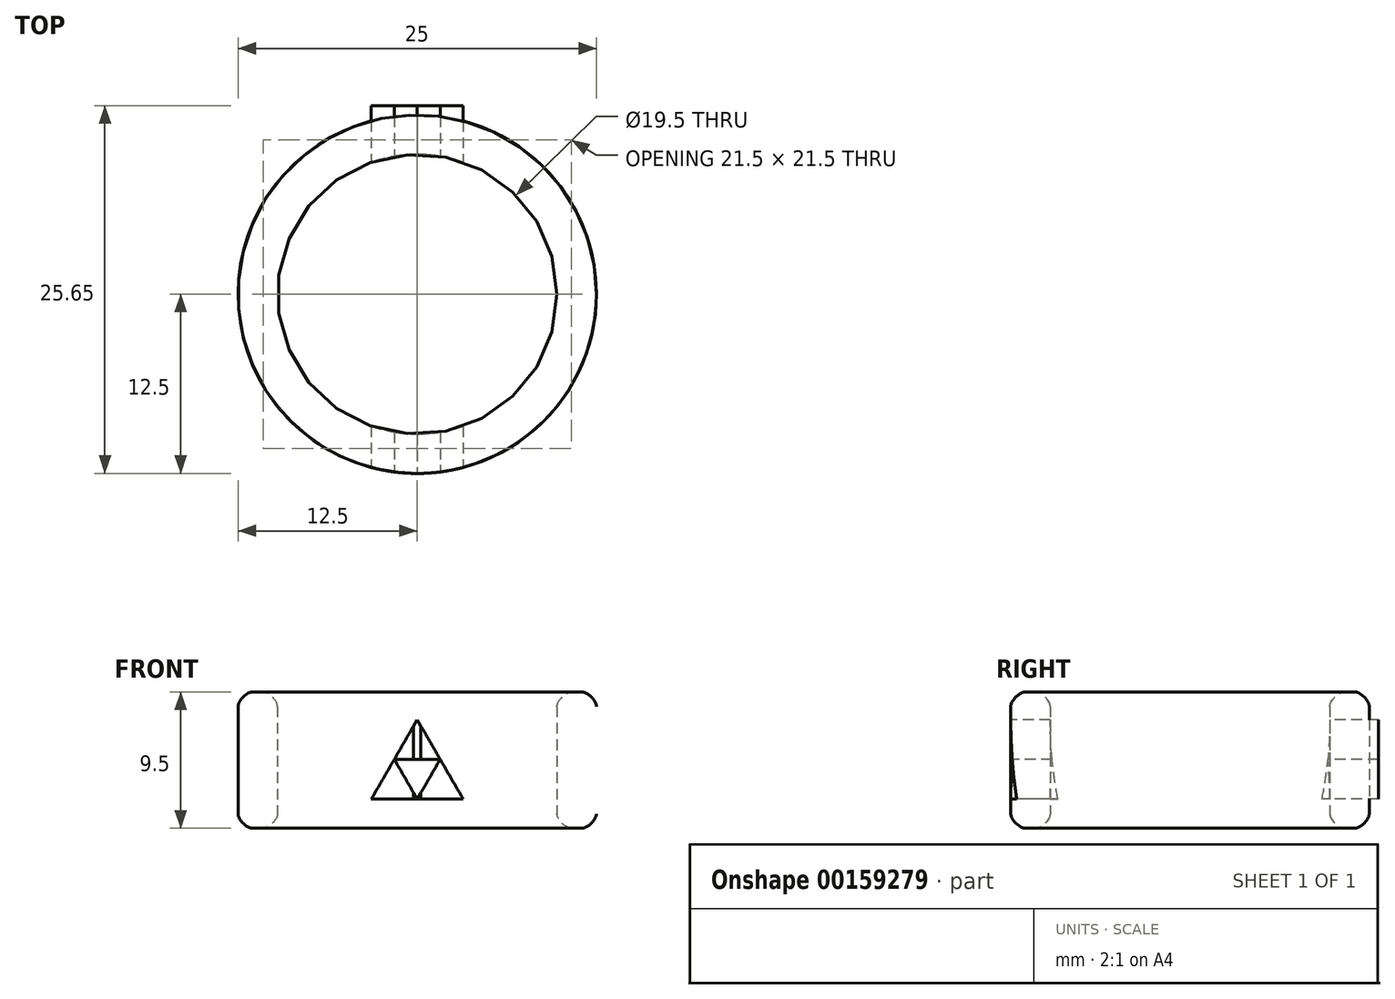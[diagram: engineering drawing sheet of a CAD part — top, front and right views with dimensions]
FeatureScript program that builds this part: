
annotation { "Feature Type Name" : "Feature", "Feature Type Description" : "" }
export const myFeature = defineFeature(function(context is Context, id is Id, definition is map)
    precondition{}
    {
        {
            var Q0;
            Q0=qCreatedBy(makeId("Top.planeOp"),FACE);
            var sketch = newSketch(context, id + "F0", { "sketchPlane" : qUnion([Q0])});
            skPoint(sketch, "E0", {"position": v(0, 12.5) * mm});
            skCircle(sketch, "E1", {"center": v(0, 12.5) * mm, "radius": 9.75 * mm});
            skCircle(sketch, "E2", {"center": v(0, 12.5) * mm, "radius": 12.5 * mm});
            skSolve(sketch);
        }
        {
            var Q0;
            Q0=makeQuery(id+"F0.imprint","IMPRINT",FACE,{"disambiguationData":[TD([[makeQuery(id+"F0.imprint","IMPRINT",EDGE,{"derivedFrom":sQuery(id+"F0.wireOp",EDGE,"E1")}),-1.0]])]});
            extrude(context, id + "F1", {"entities" : qUnion([Q0]), "depth" : 9.5 * mm});
        }
        {
            var Q0;
            Q0=makeQuery(id+"F1.opExtrude","CAP_EDGE",EDGE,{"disambiguationData":[OSD([sQuery(id+"F0.wireOp",EDGE,"E2")])],"isStart":false});
            var Q1;
            Q1=makeQuery(id+"F1.opExtrude","CAP_EDGE",EDGE,{"disambiguationData":[OSD([sQuery(id+"F0.wireOp",EDGE,"E1")])],"isStart":false});
            var Q2;
            Q2=makeQuery(id+"F1.opExtrude","CAP_EDGE",EDGE,{"disambiguationData":[OSD([sQuery(id+"F0.wireOp",EDGE,"E1")])],"isStart":true});
            var Q3;
            Q3=makeQuery(id+"F1.opExtrude","CAP_EDGE",EDGE,{"disambiguationData":[OSD([sQuery(id+"F0.wireOp",EDGE,"E2")])],"isStart":true});
            fillet(context, id + "F2", {"entities" : qUnion([Q0, Q1, Q2, Q3]), "radius" : 1 * mm, "rho" : 0.3, "crossSection" : FilletCrossSection.CONIC, "allowEdgeOverflow" : false});
        }
        {
            var Q0;
            Q0=qCreatedBy(makeId("Front.planeOp"),FACE);
            var sketch = newSketch(context, id + "F3", { "sketchPlane" : qUnion([Q0])});
            skPoint(sketch, "E3", {"position": v(0, 3.88) * mm});
            skCircle(sketch, "E4.cCircle", {"center": v(0, 3.88) * mm, "radius": 1.85 * mm, "construction": true});
            skLineSegment(sketch, "E4.0", {"start": v(3.2, 2.03) * mm, "end": v(-3.2, 2.03) * mm});
            skLineSegment(sketch, "E4.1", {"start": v(-3.2, 2.03) * mm, "end": v(0, 7.58) * mm});
            skLineSegment(sketch, "E4.2", {"start": v(0, 7.58) * mm, "end": v(3.2, 2.03) * mm});
            skPoint(sketch, "E4.0.midPoint", {"position": v(0, 2.03) * mm});
            skCircle(sketch, "E5.cCircle", {"center": v(0, 3.88) * mm, "radius": 0.92 * mm, "construction": true});
            skPoint(sketch, "E5.cCircle.perimeterSnap0", {"position": v(-1.6, 4.8) * mm});
            skLineSegment(sketch, "E5.0", {"start": v(-1.6, 4.8) * mm, "end": v(1.6, 4.8) * mm});
            skLineSegment(sketch, "E5.1", {"start": v(1.6, 4.8) * mm, "end": v(0, 2.03) * mm});
            skLineSegment(sketch, "E5.2", {"start": v(0, 2.03) * mm, "end": v(-1.6, 4.8) * mm});
            skPoint(sketch, "E5.0.midPoint", {"position": v(0, 4.8) * mm});
            skPoint(sketch, "E5.0.midPoint.positionSnap0", {"position": v(-1.6, 4.8) * mm});
            skSolve(sketch);
        }
        {
            var Q0;
            {var subQ3=sQuery(id+"F3.wireOp",EDGE,"E5.1");Q0=makeQuery(id+"F3.imprint","IMPRINT",FACE,{"disambiguationData":[TD([[makeQuery(id+"F3.imprint","IMPRINT",EDGE,{"derivedFrom":subQ3}),1.0]])]});}
            var Q1;
            {var subQ3=sQuery(id+"F3.wireOp",EDGE,"E5.0");Q1=makeQuery(id+"F3.imprint","IMPRINT",FACE,{"disambiguationData":[TD([[makeQuery(id+"F3.imprint","IMPRINT",EDGE,{"derivedFrom":subQ3}),1.0]])]});}
            var Q2;
            {var subQ3=sQuery(id+"F3.wireOp",EDGE,"E5.2");Q2=makeQuery(id+"F3.imprint","IMPRINT",FACE,{"disambiguationData":[TD([[makeQuery(id+"F3.imprint","IMPRINT",EDGE,{"derivedFrom":subQ3}),1.0]])]});}
            extrude(context, id + "F4", {"entities" : qUnion([Q0, Q1, Q2]), "oppositeDirection" : true, "depth" : 25.65 * mm});
        }
        {
            var Q0;
            Q0=qCreatedBy(makeId("Top.planeOp"),FACE);
            var sketch = newSketch(context, id + "F5", { "sketchPlane" : qUnion([Q0])});
            skCircle(sketch, "E6", {"center": v(0, 12.5) * mm, "radius": 9.75 * mm});
            skArc(sketch, "E7", {"start": v(-10.54, 5.78) * mm, "mid": v(0.2, 0) * mm, "end": v(10.76, 6.13) * mm});
            skArc(sketch, "E8", {"start": v(12.8, 4.91) * mm, "mid": v(0.13, -2.39) * mm, "end": v(-12.67, 4.68) * mm});
            skLineSegment(sketch, "E9", {"start": v(-12.67, 4.68) * mm, "end": v(-10.54, 5.78) * mm});
            skLineSegment(sketch, "E10", {"start": v(12.8, 4.91) * mm, "end": v(10.76, 6.13) * mm});
            skSolve(sketch);
        }
        {
            var Q0;
            Q0=makeQuery(id+"F5.imprint","IMPRINT",FACE,{"disambiguationData":[TD([[makeQuery(id+"F5.imprint","IMPRINT",EDGE,{"derivedFrom":sQuery(id+"F5.wireOp",EDGE,"E6")}),1.0]])]});
            var Q1;
            Q1=makeQuery(id+"F5.imprint","IMPRINT",FACE,{"disambiguationData":[TD([[makeQuery(id+"F5.imprint","IMPRINT",EDGE,{"derivedFrom":sQuery(id+"F5.wireOp",EDGE,"E7")}),-1.0]])]});
            extrude(context, id + "F6", {"entities" : qUnion([Q0, Q1]), "operationType" : NewBodyOperationType.REMOVE, "depth" : 25.4 * mm});
        }
    });
